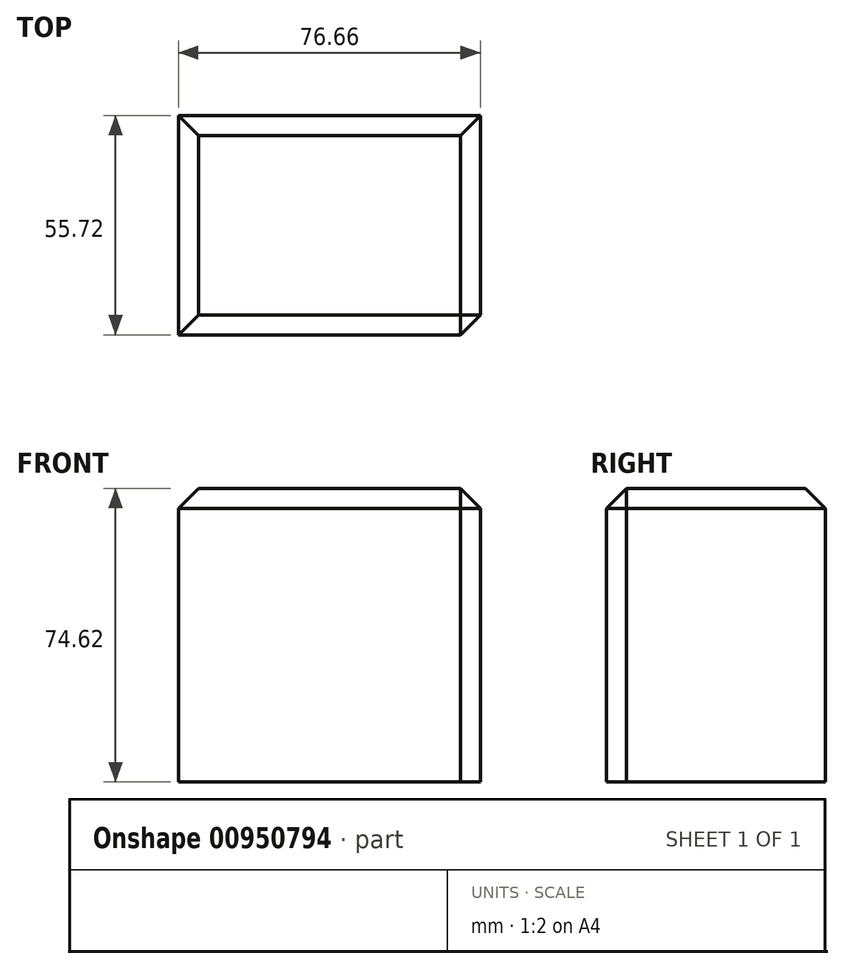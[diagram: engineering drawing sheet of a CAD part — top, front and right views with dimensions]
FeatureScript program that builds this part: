
annotation { "Feature Type Name" : "Feature", "Feature Type Description" : "" }
export const myFeature = defineFeature(function(context is Context, id is Id, definition is map)
    precondition{}
    {
        {
            var Q0;
            Q0=qCreatedBy(makeId("Front.planeOp"),FACE);
            var sketch = newSketch(context, id + "F0", { "sketchPlane" : qUnion([Q0])});
            skLineSegment(sketch, "E0.bottom", {"start": v(0, 37.3) * mm, "end": v(76.66, 37.3) * mm});
            skLineSegment(sketch, "E0.top", {"start": v(0, -37.3) * mm, "end": v(76.66, -37.3) * mm});
            skLineSegment(sketch, "E0.left", {"start": v(0, 37.3) * mm, "end": v(0, -37.3) * mm});
            skLineSegment(sketch, "E0.right", {"start": v(76.66, 37.3) * mm, "end": v(76.66, -37.3) * mm});
            skPoint(sketch, "E0.middle", {"position": v(38.33, 0) * mm});
            skSolve(sketch);
        }
        {
            var Q0;
            Q0 = qSketchRegion(id + "F0", true);
            extrude(context, id + "F1", {"entities" : qUnion([Q0]), "endBound" : BoundingType.SYMMETRIC, "oppositeDirection" : true, "depth" : 55.7 * mm, "offsetDistance" : 25.4 * mm});
        }
        {
            var Q0;
            Q0=makeQuery(id+"F1.opExtrude","SWEPT_EDGE",EDGE,{"disambiguationData":[OSD([sQuery(id+"F0.wireOp",EDGE,"E0.bottom"),sQuery(id+"F0.wireOp",EDGE,"E0.right")])]});
            var Q1;
            Q1=makeQuery(id+"F1.opExtrude","CAP_EDGE",EDGE,{"disambiguationData":[OSD([sQuery(id+"F0.wireOp",EDGE,"E0.bottom")])],"isStart":true});
            var Q2;
            Q2=makeQuery(id+"F1.opExtrude","SWEPT_EDGE",EDGE,{"disambiguationData":[OSD([sQuery(id+"F0.wireOp",EDGE,"E0.bottom"),sQuery(id+"F0.wireOp",EDGE,"E0.left")])]});
            var Q3;
            Q3=makeQuery(id+"F1.opExtrude","CAP_EDGE",EDGE,{"disambiguationData":[OSD([sQuery(id+"F0.wireOp",EDGE,"E0.right")])],"isStart":true});
            var Q4;
            Q4=makeQuery(id+"F1.opExtrude","CAP_EDGE",EDGE,{"disambiguationData":[OSD([sQuery(id+"F0.wireOp",EDGE,"E0.bottom")])],"isStart":false});
            chamfer(context, id + "F2", {"entities" : qUnion([Q0, Q1, Q2, Q3, Q4]), "width" : 5.08 * mm, "tangentPropagation" : true});
        }
    });
